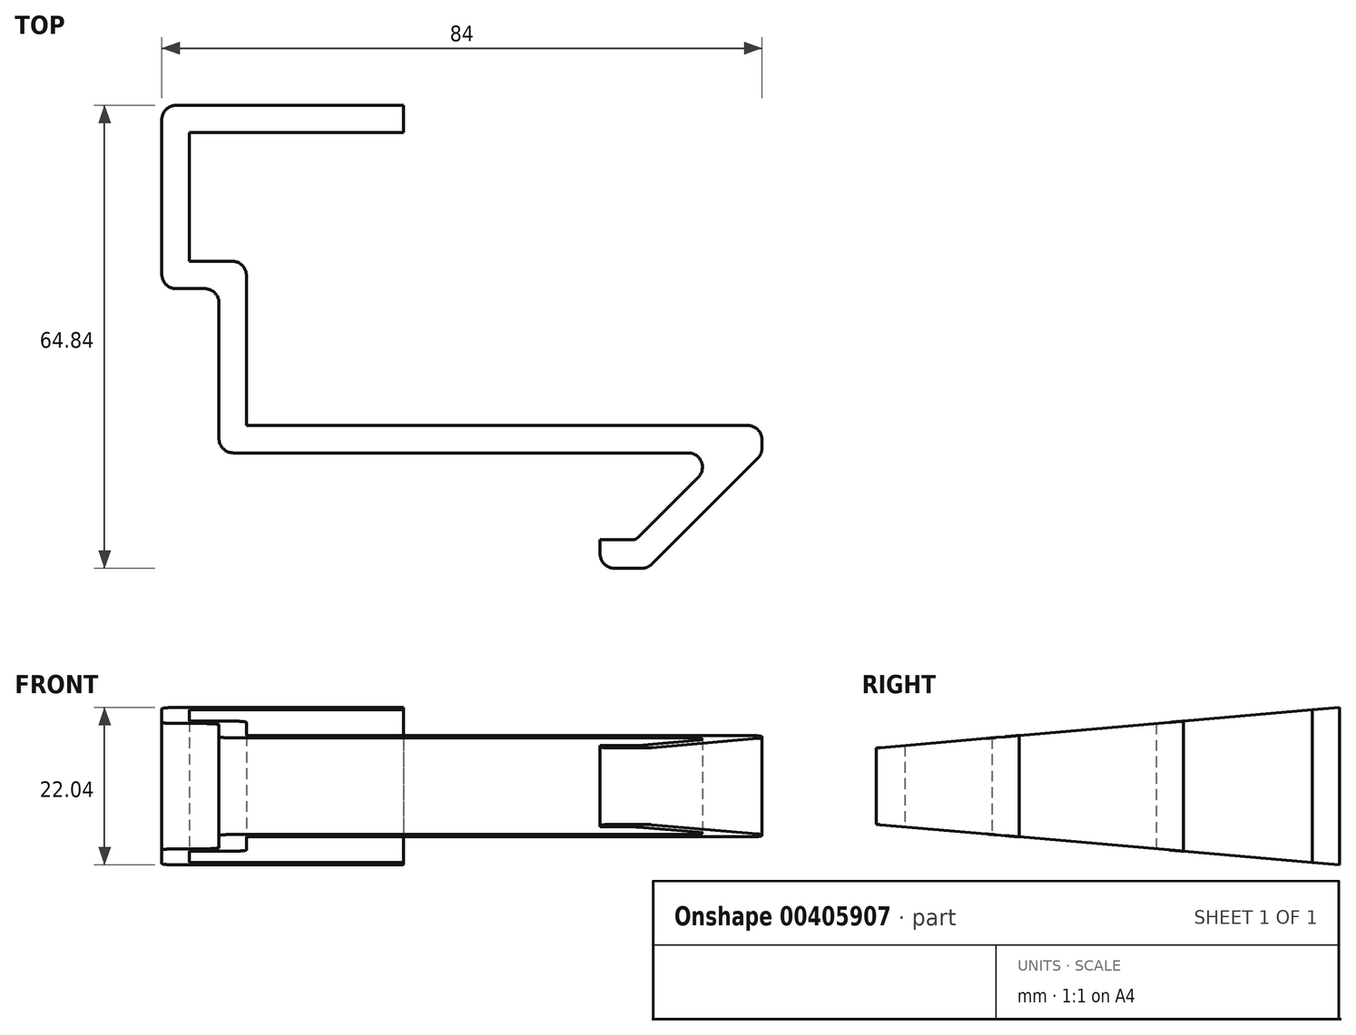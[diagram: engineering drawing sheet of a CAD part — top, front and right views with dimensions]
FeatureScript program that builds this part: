
annotation { "Feature Type Name" : "Feature", "Feature Type Description" : "" }
export const myFeature = defineFeature(function(context is Context, id is Id, definition is map)
    precondition{}
    {
        {
            var Q0;
            Q0=qCreatedBy(makeId("Top.planeOp"),FACE);
            var sketch = newSketch(context, id + "F0", { "sketchPlane" : qUnion([Q0])});
            skLineSegment(sketch, "E0", {"start": v(-10.16, 23) * mm, "end": v(-10.16, 41) * mm});
            skLineSegment(sketch, "E1", {"start": v(-10.16, 41) * mm, "end": v(19.84, 41) * mm});
            skLineSegment(sketch, "E2", {"start": v(-2.16, 0) * mm, "end": v(70, 0) * mm});
            skLineSegment(sketch, "E3", {"start": v(70, 0) * mm, "end": v(70, -4) * mm});
            skLineSegment(sketch, "E4", {"start": v(70, -4) * mm, "end": v(54, -20) * mm});
            skLineSegment(sketch, "E5", {"start": v(54, -20) * mm, "end": v(47.34, -20) * mm});
            skLineSegment(sketch, "E6", {"start": v(47.34, -20) * mm, "end": v(47.34, -16) * mm});
            skLineSegment(sketch, "E7", {"start": v(47.34, -16) * mm, "end": v(51.93, -16) * mm});
            skLineSegment(sketch, "E8", {"start": v(52.64, -15.7) * mm, "end": v(64.5, -3.84) * mm});
            skPoint(sketch, "E9.visualSharp", {"position": v(52.34, -16) * mm});
            skArc(sketch, "E9.filletArc", {"start": v(51.93, -16) * mm, "mid": v(52.31, -15.92) * mm, "end": v(52.64, -15.7) * mm});
            skPoint(sketch, "E10", {"position": v(-10.16, 23) * mm});
            skLineSegment(sketch, "E11", {"start": v(-10.16, 23) * mm, "end": v(-2.16, 23) * mm});
            skLineSegment(sketch, "E12", {"start": v(-2.16, 23) * mm, "end": v(-2.16, 0) * mm});
            skLineSegment(sketch, "E13.0", {"start": v(-14, 44.84) * mm, "end": v(19.84, 44.84) * mm});
            skLineSegment(sketch, "E13.1", {"start": v(-6, -3.84) * mm, "end": v(64.5, -3.84) * mm});
            skLineSegment(sketch, "E13.2", {"start": v(-6, 19.16) * mm, "end": v(-6, -3.84) * mm});
            skLineSegment(sketch, "E13.3", {"start": v(-14, 19.16) * mm, "end": v(-6, 19.16) * mm});
            skLineSegment(sketch, "E13.4", {"start": v(-14, 19.16) * mm, "end": v(-14, 44.84) * mm});
            skLineSegment(sketch, "E14", {"start": v(19.84, 41) * mm, "end": v(19.84, 44.84) * mm});
            skSolve(sketch);
        }
        {
            var Q0;
            Q0=makeQuery(id+"F0.imprint","IMPRINT",FACE,{"disambiguationData":[TD([[makeQuery(id+"F0.imprint","IMPRINT",EDGE,{"derivedFrom":sQuery(id+"F0.wireOp",EDGE,"E0")}),1.0]])]});
            extrude(context, id + "F1", {"entities" : qUnion([Q0]), "endBound" : BoundingType.SYMMETRIC, "depth" : 60 * mm});
        }
        {
            var Q0;
            Q0=makeQuery(id+"F1.opExtrude","SWEPT_FACE",FACE,{"disambiguationData":[OSD([sQuery(id+"F0.wireOp",EDGE,"E6")])]});
            var sketch = newSketch(context, id + "F2", { "sketchPlane" : qUnion([Q0])});
            skLineSegment(sketch, "E15", {"start": v(20, 5.35) * mm, "end": v(16, 5.35) * mm});
            skLineSegment(sketch, "E16", {"start": v(20, 5.35) * mm, "end": v(16, 5.35) * mm, "construction": true});
            skSolve(sketch);
        }
        {
            var Q0;
            Q0=makeQuery(id+"F1.opExtrude","SWEPT_FACE",FACE,{"disambiguationData":[OSD([sQuery(id+"F0.wireOp",EDGE,"E5")])]});
            var sketch = newSketch(context, id + "F3", { "sketchPlane" : qUnion([Q0])});
            skPoint(sketch, "E17.0", {"position": v(47.34, 5.35) * mm});
            skLineSegment(sketch, "E18", {"start": v(47.34, 5.35) * mm, "end": v(54, 5.35) * mm});
            skSolve(sketch);
        }
        {
            var Q0;
            Q0=sQuery(id+"F3.wireOp",EDGE,"E18");
            cPlane(context, id + "F4", {"entities" : qUnion([Q0]), "cplaneType" : CPlaneType.LINE_ANGLE, "offset" : 25 * mm, "angle" : 95 * degree, "width" : 150 * mm, "height" : 150 * mm});
        }
        {
            var Q0;
            Q0=makeQuery(id+"F1.opExtrude","CAP_FACE",FACE,{"disambiguationData":[OSD([sQuery(id+"F0.wireOp",EDGE,"E0"),sQuery(id+"F0.wireOp",EDGE,"E1"),sQuery(id+"F0.wireOp",EDGE,"E2"),sQuery(id+"F0.wireOp",EDGE,"c2f5ba21-16f8-4b23-a17a-c6d4a2f03e77.0"),sQuery(id+"F0.wireOp",EDGE,"c4762600-bb0a-4a6f-b9ea-d104176728e3.0"),sQuery(id+"F0.wireOp",EDGE,"41806372-b63f-4f5c-9e77-3c65b63a8523.0"),sQuery(id+"F0.wireOp",EDGE,"gYj7pcMZ-xCJL-o5nX-tqu4-Z78HjV7Y7173"),sQuery(id+"F0.wireOp",EDGE,"E3"),sQuery(id+"F0.wireOp",EDGE,"E4"),sQuery(id+"F0.wireOp",EDGE,"E5"),sQuery(id+"F0.wireOp",EDGE,"E6"),sQuery(id+"F0.wireOp",EDGE,"E7"),sQuery(id+"F0.wireOp",EDGE,"E8"),sQuery(id+"F0.wireOp",EDGE,"E9.filletArc")])],"isStart":false});
            var Q1;
            Q1=qCreatedBy(id+"F4.planeOp",FACE);
            extrude(context, id + "F5", {"entities" : qUnion([Q0]), "operationType" : NewBodyOperationType.REMOVE, "endBound" : BoundingType.UP_TO_SURFACE, "oppositeDirection" : true, "endBoundEntityFace" : qUnion([Q1]), "depth" : 25 * mm});
        }
        {
            var Q0;
            Q0=makeQuery(id+"F1.opExtrude","CAP_FACE",FACE,{"disambiguationData":[OSD([sQuery(id+"F0.wireOp",EDGE,"E0"),sQuery(id+"F0.wireOp",EDGE,"E1"),sQuery(id+"F0.wireOp",EDGE,"E2"),sQuery(id+"F0.wireOp",EDGE,"c2f5ba21-16f8-4b23-a17a-c6d4a2f03e77.0"),sQuery(id+"F0.wireOp",EDGE,"c4762600-bb0a-4a6f-b9ea-d104176728e3.0"),sQuery(id+"F0.wireOp",EDGE,"41806372-b63f-4f5c-9e77-3c65b63a8523.0"),sQuery(id+"F0.wireOp",EDGE,"gYj7pcMZ-xCJL-o5nX-tqu4-Z78HjV7Y7173"),sQuery(id+"F0.wireOp",EDGE,"E3"),sQuery(id+"F0.wireOp",EDGE,"E4"),sQuery(id+"F0.wireOp",EDGE,"E5"),sQuery(id+"F0.wireOp",EDGE,"E6"),sQuery(id+"F0.wireOp",EDGE,"E7"),sQuery(id+"F0.wireOp",EDGE,"E8"),sQuery(id+"F0.wireOp",EDGE,"E9.filletArc")])],"isStart":true});
            var Q1;
            Q1=qCreatedBy(makeId("Top.planeOp"),FACE);
            extrude(context, id + "F6", {"entities" : qUnion([Q0]), "operationType" : NewBodyOperationType.REMOVE, "endBound" : BoundingType.UP_TO_SURFACE, "oppositeDirection" : true, "endBoundEntityFace" : qUnion([Q1]), "depth" : 25 * mm});
        }
        {
            var Q0;
            Q0=makeQuery(id+"F1.opExtrude","SWEPT_BODY",BODY,{"disambiguationData":[OSD([sQuery(id+"F0.wireOp",EDGE,"E0"),sQuery(id+"F0.wireOp",EDGE,"E1"),sQuery(id+"F0.wireOp",EDGE,"E2"),sQuery(id+"F0.wireOp",EDGE,"c2f5ba21-16f8-4b23-a17a-c6d4a2f03e77.0"),sQuery(id+"F0.wireOp",EDGE,"c4762600-bb0a-4a6f-b9ea-d104176728e3.0"),sQuery(id+"F0.wireOp",EDGE,"41806372-b63f-4f5c-9e77-3c65b63a8523.0"),sQuery(id+"F0.wireOp",EDGE,"gYj7pcMZ-xCJL-o5nX-tqu4-Z78HjV7Y7173"),sQuery(id+"F0.wireOp",EDGE,"E3"),sQuery(id+"F0.wireOp",EDGE,"E4"),sQuery(id+"F0.wireOp",EDGE,"E5"),sQuery(id+"F0.wireOp",EDGE,"E6"),sQuery(id+"F0.wireOp",EDGE,"E7"),sQuery(id+"F0.wireOp",EDGE,"E8"),sQuery(id+"F0.wireOp",EDGE,"E9.filletArc")])]});
            var Q1;
            Q1=qCreatedBy(makeId("Top.planeOp"),FACE);
            mirror(context, id + "F7", {"operationType" : NewBodyOperationType.ADD, "entities" : qUnion([Q0]), "mirrorPlane" : qUnion([Q1])});
        }
        {
            var Q0;
            Q0=makeQuery(id+"F1.opExtrude","SWEPT_EDGE",EDGE,{"disambiguationData":[OSD([sQuery(id+"F0.wireOp",EDGE,"E2"),sQuery(id+"F0.wireOp",EDGE,"E3")])]});
            var Q1;
            Q1=makeQuery(id+"F1.opExtrude","SWEPT_EDGE",EDGE,{"disambiguationData":[OSD([sQuery(id+"F0.wireOp",EDGE,"E3"),sQuery(id+"F0.wireOp",EDGE,"E4")])]});
            var Q2;
            Q2=makeQuery(id+"F1.opExtrude","SWEPT_EDGE",EDGE,{"disambiguationData":[OSD([sQuery(id+"F0.wireOp",EDGE,"c4762600-bb0a-4a6f-b9ea-d104176728e3.0"),sQuery(id+"F0.wireOp",EDGE,"E8")])]});
            var Q3;
            Q3=makeQuery(id+"F1.opExtrude","SWEPT_EDGE",EDGE,{"disambiguationData":[OSD([sQuery(id+"F0.wireOp",EDGE,"E4"),sQuery(id+"F0.wireOp",EDGE,"E5")])]});
            var Q4;
            Q4=makeQuery(id+"F1.opExtrude","SWEPT_EDGE",EDGE,{"disambiguationData":[OSD([sQuery(id+"F0.wireOp",EDGE,"E5"),sQuery(id+"F0.wireOp",EDGE,"E6")])]});
            fillet(context, id + "F8", {"entities" : qUnion([Q0, Q1, Q2, Q3, Q4]), "radius" : 2 * mm, "tangentPropagation" : true, "allowEdgeOverflow" : false});
        }
        {
            var Q0;
            {var subQ0=makeQuery(id+"F1.opExtrude","SWEPT_EDGE",EDGE,{"disambiguationData":[OSD([sQuery(id+"F0.wireOp",EDGE,"E13.0"),sQuery(id+"F0.wireOp",EDGE,"E13.4")])]});Q0=makeQuery(id+"F7.boolean.opBoolean","MERGE",EDGE,{"derivedFrom":[subQ0,makeQuery(id+"F7.opPattern","COPY",EDGE,{"derivedFrom":subQ0,"instanceName":"1"})]});}
            var Q1;
            {var subQ0=makeQuery(id+"F1.opExtrude","SWEPT_EDGE",EDGE,{"disambiguationData":[OSD([sQuery(id+"F0.wireOp",EDGE,"E13.3"),sQuery(id+"F0.wireOp",EDGE,"E13.4")])]});Q1=makeQuery(id+"F7.boolean.opBoolean","MERGE",EDGE,{"derivedFrom":[subQ0,makeQuery(id+"F7.opPattern","COPY",EDGE,{"derivedFrom":subQ0,"instanceName":"1"})]});}
            var Q2;
            {var subQ0=makeQuery(id+"F1.opExtrude","SWEPT_EDGE",EDGE,{"disambiguationData":[OSD([sQuery(id+"F0.wireOp",EDGE,"E13.2"),sQuery(id+"F0.wireOp",EDGE,"E13.3")])]});Q2=makeQuery(id+"F7.boolean.opBoolean","MERGE",EDGE,{"derivedFrom":[subQ0,makeQuery(id+"F7.opPattern","COPY",EDGE,{"derivedFrom":subQ0,"instanceName":"1"})]});}
            var Q3;
            {var subQ0=makeQuery(id+"F1.opExtrude","SWEPT_EDGE",EDGE,{"disambiguationData":[OSD([sQuery(id+"F0.wireOp",EDGE,"E13.1"),sQuery(id+"F0.wireOp",EDGE,"E13.2")])]});Q3=makeQuery(id+"F7.boolean.opBoolean","MERGE",EDGE,{"derivedFrom":[subQ0,makeQuery(id+"F7.opPattern","COPY",EDGE,{"derivedFrom":subQ0,"instanceName":"1"})]});}
            var Q4;
            {var subQ0=makeQuery(id+"F1.opExtrude","SWEPT_EDGE",EDGE,{"disambiguationData":[OSD([sQuery(id+"F0.wireOp",EDGE,"E11"),sQuery(id+"F0.wireOp",EDGE,"E12")])]});Q4=makeQuery(id+"F7.boolean.opBoolean","MERGE",EDGE,{"derivedFrom":[subQ0,makeQuery(id+"F7.opPattern","COPY",EDGE,{"derivedFrom":subQ0,"instanceName":"1"})]});}
            fillet(context, id + "F9", {"entities" : qUnion([Q0, Q1, Q2, Q3, Q4]), "radius" : 2 * mm, "tangentPropagation" : true, "allowEdgeOverflow" : false});
        }
    });
